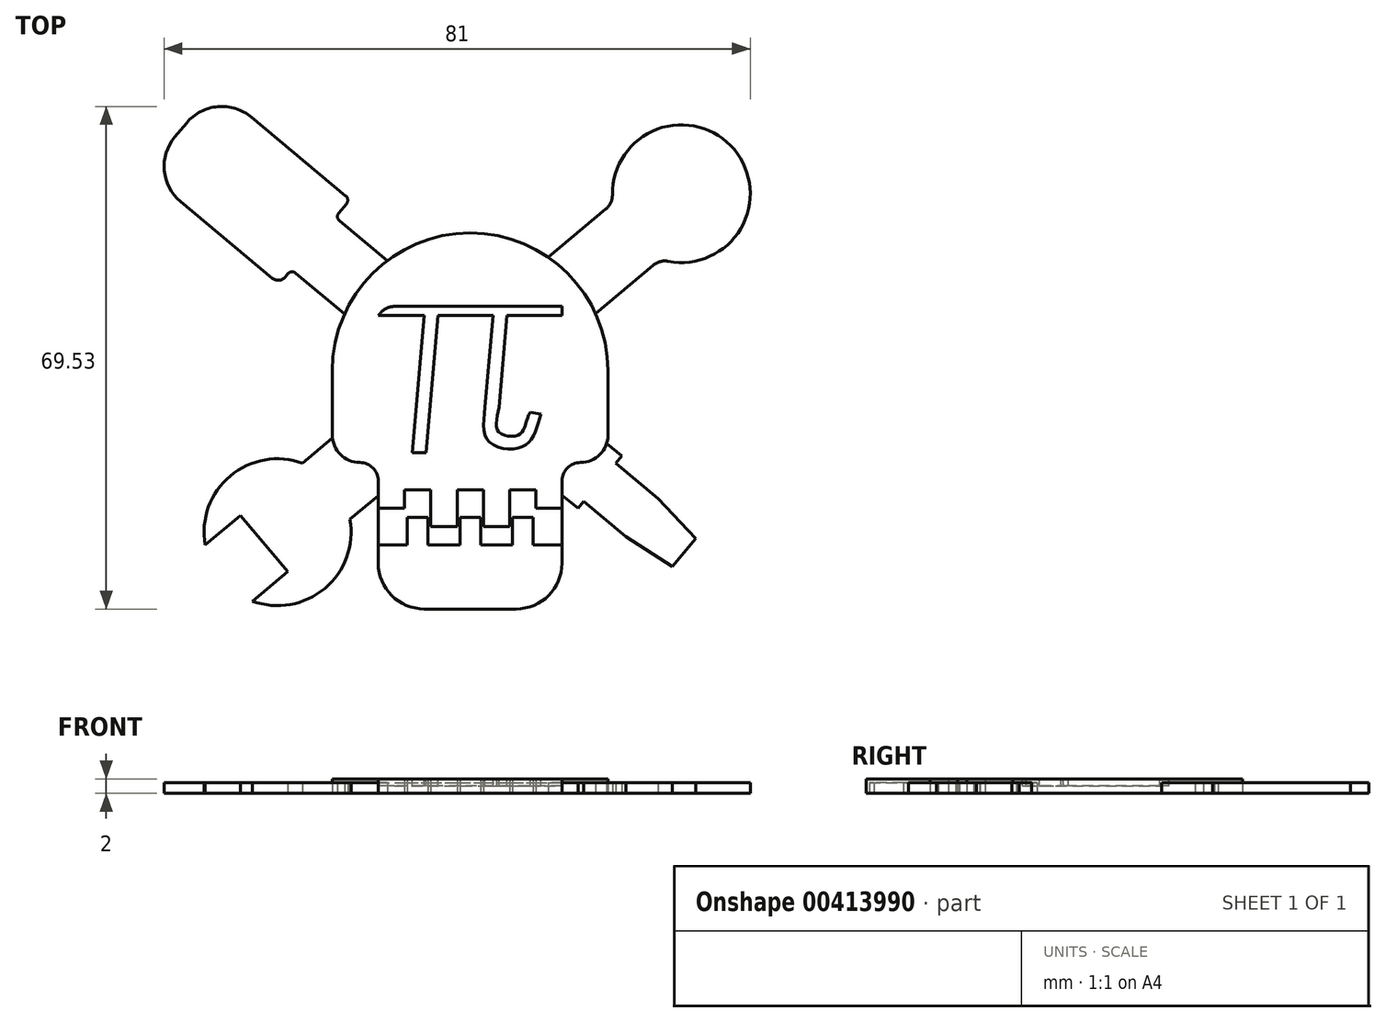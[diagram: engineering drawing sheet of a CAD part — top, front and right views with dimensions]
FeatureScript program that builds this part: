
annotation { "Feature Type Name" : "Feature", "Feature Type Description" : "" }
export const myFeature = defineFeature(function(context is Context, id is Id, definition is map)
    precondition{}
    {
        {
            var Q0;
            Q0=qCreatedBy(makeId("Top.planeOp"),FACE);
            var sketch = newSketch(context, id + "F0", { "sketchPlane" : qUnion([Q0])});
            skLineSegment(sketch, "E0.bottom", {"start": v(0, 19.05) * mm, "end": v(0, 19.05) * mm});
            skLineSegment(sketch, "E0.left", {"start": v(-19.05, 0) * mm, "end": v(-19.05, -8.9) * mm});
            skLineSegment(sketch, "E0.right", {"start": v(19.05, 0) * mm, "end": v(19.05, -8.9) * mm});
            skPoint(sketch, "E0.middle", {"position": v(0, 0) * mm});
            skPoint(sketch, "E1.visualSharp", {"position": v(-19.05, 19.05) * mm});
            skArc(sketch, "E1.filletArc", {"start": v(0, 19.05) * mm, "mid": v(-13.47, 13.47) * mm, "end": v(-19.05, 0) * mm});
            skPoint(sketch, "E2.visualSharp", {"position": v(19.05, 19.05) * mm});
            skArc(sketch, "E2.filletArc", {"start": v(19.05, 0) * mm, "mid": v(13.47, 13.47) * mm, "end": v(0, 19.05) * mm});
            skPoint(sketch, "E3", {"position": v(-19.05, -12.7) * mm});
            skPoint(sketch, "E4", {"position": v(19.05, -12.7) * mm});
            skLineSegment(sketch, "E5", {"start": v(-15.24, -12.7) * mm, "end": v(-15.24, -12.7) * mm});
            skLineSegment(sketch, "E6", {"start": v(15.24, -12.7) * mm, "end": v(15.24, -12.7) * mm});
            skLineSegment(sketch, "E7", {"start": v(-12.7, -15.24) * mm, "end": v(-12.7, -19.05) * mm});
            skLineSegment(sketch, "E8", {"start": v(12.7, -15.24) * mm, "end": v(12.7, -19.05) * mm});
            skArc(sketch, "E9.filletArc", {"start": v(-19.05, -8.9) * mm, "mid": v(-17.93, -11.58) * mm, "end": v(-15.24, -12.7) * mm});
            skArc(sketch, "E10.filletArc", {"start": v(15.24, -12.7) * mm, "mid": v(17.93, -11.58) * mm, "end": v(19.05, -8.9) * mm});
            skPoint(sketch, "E11.visualSharp", {"position": v(-12.7, -12.7) * mm});
            skArc(sketch, "E11.filletArc", {"start": v(-12.7, -15.24) * mm, "mid": v(-13.44, -13.44) * mm, "end": v(-15.24, -12.7) * mm});
            skPoint(sketch, "E12.visualSharp", {"position": v(12.7, -12.7) * mm});
            skArc(sketch, "E12.filletArc", {"start": v(15.24, -12.7) * mm, "mid": v(13.44, -13.44) * mm, "end": v(12.7, -15.24) * mm});
            skLineSegment(sketch, "E13", {"start": v(-12.7, -19.05) * mm, "end": v(-9.07, -19.05) * mm});
            skLineSegment(sketch, "E14", {"start": v(-5.44, -21.6) * mm, "end": v(-1.8, -21.6) * mm});
            skLineSegment(sketch, "E15", {"start": v(1.83, -21.6) * mm, "end": v(5.46, -21.6) * mm});
            skLineSegment(sketch, "E16", {"start": v(9.1, -19.05) * mm, "end": v(12.7, -19.05) * mm});
            skLineSegment(sketch, "E17", {"start": v(-9.07, -19.05) * mm, "end": v(-9.07, -16.51) * mm});
            skLineSegment(sketch, "E18", {"start": v(-9.07, -16.51) * mm, "end": v(-5.44, -16.51) * mm});
            skLineSegment(sketch, "E19", {"start": v(-5.44, -16.51) * mm, "end": v(-5.44, -21.6) * mm});
            skLineSegment(sketch, "E20", {"start": v(-1.8, -21.6) * mm, "end": v(-1.8, -16.51) * mm});
            skLineSegment(sketch, "E21", {"start": v(-1.8, -16.51) * mm, "end": v(1.83, -16.51) * mm});
            skLineSegment(sketch, "E22", {"start": v(1.83, -16.51) * mm, "end": v(1.83, -21.6) * mm});
            skLineSegment(sketch, "E23", {"start": v(5.46, -21.6) * mm, "end": v(5.46, -16.51) * mm});
            skLineSegment(sketch, "E24", {"start": v(5.46, -16.51) * mm, "end": v(9.1, -16.51) * mm});
            skLineSegment(sketch, "E25", {"start": v(9.1, -16.51) * mm, "end": v(9.1, -19.05) * mm});
            skLineSegment(sketch, "E26", {"start": v(25.29, 14.59) * mm, "end": v(-16.62, -20.58) * mm});
            skLineSegment(sketch, "E27", {"start": v(-23.15, -12.8) * mm, "end": v(18.76, 22.37) * mm});
            skLineSegment(sketch, "E28", {"start": v(-24.1, 13.5) * mm, "end": v(14.9, -19.05) * mm});
            skLineSegment(sketch, "E29", {"start": v(20.94, -11.8) * mm, "end": v(-18.06, 20.74) * mm});
            skPoint(sketch, "E30", {"position": v(29.19, 24.5) * mm});
            skArc(sketch, "E31", {"start": v(27.4, 15.13) * mm, "mid": v(36.48, 30.61) * mm, "end": v(19.66, 24.35) * mm});
            skPoint(sketch, "E32.visualSharp", {"position": v(19.75, 23.2) * mm});
            skArc(sketch, "E32.filletArc", {"start": v(18.76, 22.37) * mm, "mid": v(19.43, 23.26) * mm, "end": v(19.66, 24.35) * mm});
            skPoint(sketch, "E33.visualSharp", {"position": v(26.28, 15.42) * mm});
            skArc(sketch, "E33.filletArc", {"start": v(27.4, 15.13) * mm, "mid": v(26.28, 15.1) * mm, "end": v(25.29, 14.59) * mm});
            skLineSegment(sketch, "E34", {"start": v(-17.19, 24.18) * mm, "end": v(-30.25, 35.09) * mm});
            skLineSegment(sketch, "E35", {"start": v(-39.2, 34.28) * mm, "end": v(-40.82, 32.33) * mm});
            skLineSegment(sketch, "E36", {"start": v(-40.01, 23.39) * mm, "end": v(-27.34, 12.8) * mm});
            skLineSegment(sketch, "E37", {"start": v(-25.55, 12.97) * mm, "end": v(-25.18, 13.4) * mm});
            skLineSegment(sketch, "E38.trimOffspring", {"start": v(-18.16, 21.82) * mm, "end": v(-17.09, 23.1) * mm});
            skPoint(sketch, "E39.visualSharp", {"position": v(-35.12, 39.16) * mm});
            skArc(sketch, "E39.filletArc", {"start": v(-30.25, 35.09) * mm, "mid": v(-34.89, 36.54) * mm, "end": v(-39.2, 34.28) * mm});
            skPoint(sketch, "E40.visualSharp", {"position": v(-44.89, 27.46) * mm});
            skArc(sketch, "E40.filletArc", {"start": v(-40.82, 32.33) * mm, "mid": v(-42.27, 27.7) * mm, "end": v(-40.01, 23.39) * mm});
            skPoint(sketch, "E41.visualSharp", {"position": v(-26.36, 12) * mm});
            skArc(sketch, "E41.filletArc", {"start": v(-27.34, 12.8) * mm, "mid": v(-26.41, 12.52) * mm, "end": v(-25.55, 12.97) * mm});
            skPoint(sketch, "E42.visualSharp", {"position": v(-24.7, 14) * mm});
            skArc(sketch, "E42.filletArc", {"start": v(-24.1, 13.5) * mm, "mid": v(-24.66, 13.68) * mm, "end": v(-25.18, 13.4) * mm});
            skPoint(sketch, "E43.visualSharp", {"position": v(-18.65, 21.24) * mm});
            skArc(sketch, "E43.filletArc", {"start": v(-18.16, 21.82) * mm, "mid": v(-18.33, 21.26) * mm, "end": v(-18.06, 20.74) * mm});
            skPoint(sketch, "E44.visualSharp", {"position": v(-16.6, 23.7) * mm});
            skArc(sketch, "E44.filletArc", {"start": v(-17.09, 23.1) * mm, "mid": v(-16.91, 23.66) * mm, "end": v(-17.19, 24.18) * mm});
            skLineSegment(sketch, "E45", {"start": v(14.9, -19.05) * mm, "end": v(20.94, -11.8) * mm});
            skLineSegment(sketch, "E46", {"start": v(20.12, -12.78) * mm, "end": v(25.97, -17.67) * mm});
            skLineSegment(sketch, "E47", {"start": v(31.2, -23.21) * mm, "end": v(27.95, -27.11) * mm});
            skLineSegment(sketch, "E48", {"start": v(21.56, -22.96) * mm, "end": v(15.7, -18.08) * mm});
            skLineSegment(sketch, "E49", {"start": v(21.56, -22.96) * mm, "end": v(27.95, -27.11) * mm});
            skLineSegment(sketch, "E50", {"start": v(25.97, -17.67) * mm, "end": v(31.2, -23.21) * mm});
            skPoint(sketch, "E51", {"position": v(17.92, -15.43) * mm});
            skArc(sketch, "E52", {"start": v(-23.15, -12.8) * mm, "mid": v(-33.15, -14.56) * mm, "end": v(-36.63, -24.1) * mm});
            skLineSegment(sketch, "E53", {"start": v(-23.15, -12.8) * mm, "end": v(-36.63, -24.1) * mm});
            skLineSegment(sketch, "E54", {"start": v(-16.62, -20.58) * mm, "end": v(-30.1, -31.89) * mm});
            skArc(sketch, "E55.trimOffspring", {"start": v(-30.1, -31.89) * mm, "mid": v(-20.1, -30.12) * mm, "end": v(-16.62, -20.58) * mm});
            skLineSegment(sketch, "E56", {"start": v(-31.76, -20.02) * mm, "end": v(-25.23, -27.8) * mm});
            skSolve(sketch);
        }
        {
            var Q0;
            {var subQ6=sQuery(id+"F0.wireOp",EDGE,"E0.left");Q0=makeQuery(id+"F0.imprint","IMPRINT",FACE,{"disambiguationData":[TD([[makeQuery(id+"F0.imprint","IMPRINT",EDGE,{"derivedFrom":subQ6}),1.0]])]});}
            var Q1;
            {var subQ6=sQuery(id+"F0.wireOp",EDGE,"E0.right");Q1=makeQuery(id+"F0.imprint","IMPRINT",FACE,{"disambiguationData":[TD([[makeQuery(id+"F0.imprint","IMPRINT",EDGE,{"derivedFrom":subQ6}),-1.0]])]});}
            var Q2;
            {var subQ0=sQuery(id+"F0.wireOp",EDGE,"E2.filletArc");var subQ1=sQuery(id+"F0.wireOp",EDGE,"E1.filletArc");var subQ2=makeQuery(id+"F0.imprint","INTERSECT",VERTEX,{"derivedFrom":[subQ1,subQ0]});Q2=makeQuery(id+"F0.imprint","IMPRINT",FACE,{"disambiguationData":[TD([[makeQuery(id+"F0.imprint","IMPRINT",EDGE,{"disambiguationData":[TD([[subQ2,-1.0]])],"derivedFrom":subQ1}),1.0]])]});}
            var Q3;
            {var subQ6=sQuery(id+"F0.wireOp",EDGE,"E13");Q3=makeQuery(id+"F0.imprint","IMPRINT",FACE,{"disambiguationData":[TD([[makeQuery(id+"F0.imprint","IMPRINT",EDGE,{"derivedFrom":subQ6}),1.0]])]});}
            var Q4;
            {var subQ0=sQuery(id+"F0.wireOp",EDGE,"E29");var subQ1=sQuery(id+"F0.wireOp",EDGE,"E1.filletArc");var subQ2=makeQuery(id+"F0.imprint","INTERSECT",VERTEX,{"derivedFrom":[subQ1,subQ0]});Q4=makeQuery(id+"F0.imprint","IMPRINT",FACE,{"disambiguationData":[TD([[makeQuery(id+"F0.imprint","IMPRINT",EDGE,{"disambiguationData":[TD([[subQ2,-1.0]])],"derivedFrom":subQ1}),1.0]])]});}
            var Q5;
            {var subQ0=sQuery(id+"F0.wireOp",EDGE,"E26");var subQ1=sQuery(id+"F0.wireOp",EDGE,"E2.filletArc");var subQ2=makeQuery(id+"F0.imprint","INTERSECT",VERTEX,{"derivedFrom":[subQ1,subQ0]});Q5=makeQuery(id+"F0.imprint","IMPRINT",FACE,{"disambiguationData":[TD([[makeQuery(id+"F0.imprint","IMPRINT",EDGE,{"disambiguationData":[TD([[subQ2,-1.0]])],"derivedFrom":subQ1}),1.0]])]});}
            var Q6;
            {var subQ5=sQuery(id+"F0.wireOp",EDGE,"E11.filletArc");Q6=makeQuery(id+"F0.imprint","IMPRINT",FACE,{"disambiguationData":[TD([[makeQuery(id+"F0.imprint","IMPRINT",EDGE,{"derivedFrom":subQ5}),-1.0]])]});}
            var Q7;
            {var subQ7=sQuery(id+"F0.wireOp",EDGE,"E12.filletArc");Q7=makeQuery(id+"F0.imprint","IMPRINT",FACE,{"disambiguationData":[TD([[makeQuery(id+"F0.imprint","IMPRINT",EDGE,{"derivedFrom":subQ7}),-1.0]])]});}
            var Q8;
            {var subQ0=sQuery(id+"F0.wireOp",EDGE,"E29");var subQ1=sQuery(id+"F0.wireOp",EDGE,"E26");var subQ2=makeQuery(id+"F0.imprint","INTERSECT",VERTEX,{"derivedFrom":[subQ1,subQ0]});Q8=makeQuery(id+"F0.imprint","IMPRINT",FACE,{"disambiguationData":[TD([[makeQuery(id+"F0.imprint","IMPRINT",EDGE,{"disambiguationData":[TD([[subQ2,-1.0]])],"derivedFrom":subQ1}),-1.0]])]});}
            extrude(context, id + "F1", {"entities" : qUnion([Q0, Q1, Q2, Q3, Q4, Q5, Q6, Q7, Q8]), "depth" : 2 * mm});
        }
        {
            var Q0;
            {var subQ1=sQuery(id+"F0.wireOp",EDGE,"E46");Q0=makeQuery(id+"F0.imprint","IMPRINT",FACE,{"disambiguationData":[TD([[makeQuery(id+"F0.imprint","IMPRINT",EDGE,{"derivedFrom":subQ1}),-1.0]])]});}
            var Q1;
            Q1=makeQuery(id+"F0.imprint","IMPRINT",FACE,{"disambiguationData":[TD([[makeQuery(id+"F0.imprint","IMPRINT",EDGE,{"derivedFrom":sQuery(id+"F0.wireOp",EDGE,"E31")}),1.0]])]});
            var Q2;
            Q2=makeQuery(id+"F0.imprint","IMPRINT",FACE,{"disambiguationData":[TD([[makeQuery(id+"F0.imprint","IMPRINT",EDGE,{"derivedFrom":sQuery(id+"F0.wireOp",EDGE,"E34")}),1.0]])]});
            var Q3;
            {var subQ5=sQuery(id+"F0.wireOp",EDGE,"E11.filletArc");Q3=makeQuery(id+"F0.imprint","IMPRINT",FACE,{"disambiguationData":[TD([[makeQuery(id+"F0.imprint","IMPRINT",EDGE,{"derivedFrom":subQ5}),1.0]])]});}
            var Q4;
            {var subQ0=sQuery(id+"F0.wireOp",EDGE,"E55.trimOffspring");Q4=makeQuery(id+"F0.imprint","IMPRINT",FACE,{"disambiguationData":[TD([[makeQuery(id+"F0.imprint","IMPRINT",EDGE,{"derivedFrom":subQ0}),1.0]])]});}
            var Q5;
            {var subQ0=sQuery(id+"F0.wireOp",EDGE,"E52");Q5=makeQuery(id+"F0.imprint","IMPRINT",FACE,{"disambiguationData":[TD([[makeQuery(id+"F0.imprint","IMPRINT",EDGE,{"derivedFrom":subQ0}),1.0]])]});}
            var Q6;
            {var subQ0=sQuery(id+"F0.wireOp",EDGE,"E12.filletArc");Q6=makeQuery(id+"F0.imprint","IMPRINT",FACE,{"disambiguationData":[TD([[makeQuery(id+"F0.imprint","IMPRINT",EDGE,{"derivedFrom":subQ0}),1.0]])]});}
            extrude(context, id + "F2", {"entities" : qUnion([Q0, Q1, Q2, Q3, Q4, Q5, Q6]), "operationType" : NewBodyOperationType.ADD, "depth" : 1.5 * mm});
        }
        {
            var Q0;
            Q0=makeQuery(id+"F1.opExtrude","CAP_FACE",FACE,{"disambiguationData":[OSD([sQuery(id+"F0.wireOp",EDGE,"E0.left"),sQuery(id+"F0.wireOp",EDGE,"E0.right"),sQuery(id+"F0.wireOp",EDGE,"E1.filletArc"),sQuery(id+"F0.wireOp",EDGE,"E2.filletArc"),sQuery(id+"F0.wireOp",EDGE,"E7"),sQuery(id+"F0.wireOp",EDGE,"E8"),sQuery(id+"F0.wireOp",EDGE,"E9.filletArc"),sQuery(id+"F0.wireOp",EDGE,"E10.filletArc"),sQuery(id+"F0.wireOp",EDGE,"E11.filletArc"),sQuery(id+"F0.wireOp",EDGE,"E12.filletArc"),sQuery(id+"F0.wireOp",EDGE,"E13"),sQuery(id+"F0.wireOp",EDGE,"E14"),sQuery(id+"F0.wireOp",EDGE,"E15"),sQuery(id+"F0.wireOp",EDGE,"E16"),sQuery(id+"F0.wireOp",EDGE,"E17"),sQuery(id+"F0.wireOp",EDGE,"E18"),sQuery(id+"F0.wireOp",EDGE,"E19"),sQuery(id+"F0.wireOp",EDGE,"E20"),sQuery(id+"F0.wireOp",EDGE,"E21"),sQuery(id+"F0.wireOp",EDGE,"E22"),sQuery(id+"F0.wireOp",EDGE,"E23"),sQuery(id+"F0.wireOp",EDGE,"E24"),sQuery(id+"F0.wireOp",EDGE,"E25")])],"isStart":false});
            var sketch = newSketch(context, id + "F3", { "sketchPlane" : qUnion([Q0])});
            skLineSegment(sketch, "E57", {"start": v(-10.45, 8.9) * mm, "end": v(12.7, 8.9) * mm});
            skLineSegment(sketch, "E58", {"start": v(12.7, 8.9) * mm, "end": v(12.7, 7.62) * mm});
            skLineSegment(sketch, "E59", {"start": v(12.7, 7.62) * mm, "end": v(5.08, 7.62) * mm});
            skLineSegment(sketch, "E60", {"start": v(-12.39, 7.99) * mm, "end": v(-12.7, 7.62) * mm});
            skPoint(sketch, "E61.visualSharp", {"position": v(-11.63, 8.9) * mm});
            skArc(sketch, "E61.filletArc", {"start": v(-10.45, 8.9) * mm, "mid": v(-11.52, 8.65) * mm, "end": v(-12.39, 7.99) * mm});
            skLineSegment(sketch, "E62", {"start": v(-4.45, 7.62) * mm, "end": v(-6.1, -11.36) * mm});
            skLineSegment(sketch, "E63", {"start": v(-6.1, -11.36) * mm, "end": v(-8.01, -11.36) * mm});
            skLineSegment(sketch, "E64", {"start": v(-8.01, -11.36) * mm, "end": v(-6.35, 7.62) * mm});
            skLineSegment(sketch, "E65", {"start": v(3.18, 7.62) * mm, "end": v(2.07, -5.03) * mm});
            skLineSegment(sketch, "E66", {"start": v(5.08, 7.62) * mm, "end": v(3.97, -5.03) * mm});
            skFitSpline(sketch, "E67", {"points": [v(2.07, -5.03) * mm, v(2.44, -9.64) * mm, v(6.19, -10.81) * mm, v(8.6, -9.29) * mm, v(9.8, -5.99) * mm], "startDerivative": vector(-2.55, -20.67) * mm, "endDerivative": vector(5.73, 14.8) * mm});
            skFitSpline(sketch, "E68", {"points": [v(3.97, -5.03) * mm, v(3.93, -8.44) * mm, v(6.62, -8.9) * mm, v(7.57, -7.69) * mm, v(8.3, -5.73) * mm], "startDerivative": vector(-1.95, -13.67) * mm, "endDerivative": vector(5.78, 10.73) * mm});
            skLineSegment(sketch, "E69", {"start": v(8.3, -5.73) * mm, "end": v(9.8, -5.99) * mm});
            skLineSegment(sketch, "E70.trimOffspring", {"start": v(-6.35, 7.62) * mm, "end": v(-12.7, 7.62) * mm});
            skLineSegment(sketch, "E71.trimOffspring", {"start": v(3.18, 7.62) * mm, "end": v(-4.44, 7.62) * mm});
            skSolve(sketch);
        }
        {
            var Q0;
            Q0 = qSketchRegion(id + "F3", true);
            extrude(context, id + "F4", {"entities" : qUnion([Q0]), "operationType" : NewBodyOperationType.REMOVE, "oppositeDirection" : true, "depth" : 1 * mm});
        }
        {
            var Q0;
            {var subQ0=sQuery(id+"F0.wireOp",EDGE,"E29");var subQ1=sQuery(id+"F0.wireOp",EDGE,"E28");var subQ2=sQuery(id+"F0.wireOp",EDGE,"E12.filletArc");var subQ3=sQuery(id+"F0.wireOp",EDGE,"E10.filletArc");var subQ4=sQuery(id+"F0.wireOp",EDGE,"E8");var subQ5=sQuery(id+"F0.wireOp",EDGE,"E27");var subQ6=sQuery(id+"F0.wireOp",EDGE,"E26");var subQ7=sQuery(id+"F0.wireOp",EDGE,"E11.filletArc");var subQ8=sQuery(id+"F0.wireOp",EDGE,"E9.filletArc");var subQ9=sQuery(id+"F0.wireOp",EDGE,"E7");var subQ10=sQuery(id+"F0.wireOp",EDGE,"E2.filletArc");var subQ11=sQuery(id+"F0.wireOp",EDGE,"E1.filletArc");Q0=makeQuery(id+"F2.boolean.opBoolean","MERGE",FACE,{"derivedFrom":[makeQuery(id+"F1.opExtrude","CAP_FACE",FACE,{"disambiguationData":[OSD([sQuery(id+"F0.wireOp",EDGE,"E0.left"),sQuery(id+"F0.wireOp",EDGE,"E0.right"),subQ11,subQ10,subQ9,subQ4,subQ8,subQ3,subQ7,subQ2,sQuery(id+"F0.wireOp",EDGE,"E13"),sQuery(id+"F0.wireOp",EDGE,"E14"),sQuery(id+"F0.wireOp",EDGE,"E15"),sQuery(id+"F0.wireOp",EDGE,"E16"),sQuery(id+"F0.wireOp",EDGE,"E17"),sQuery(id+"F0.wireOp",EDGE,"E18"),sQuery(id+"F0.wireOp",EDGE,"E19"),sQuery(id+"F0.wireOp",EDGE,"E20"),sQuery(id+"F0.wireOp",EDGE,"E21"),sQuery(id+"F0.wireOp",EDGE,"E22"),sQuery(id+"F0.wireOp",EDGE,"E23"),sQuery(id+"F0.wireOp",EDGE,"E24"),sQuery(id+"F0.wireOp",EDGE,"E25")])],"isStart":true}),makeQuery(id+"F2.opExtrude","CAP_FACE",FACE,{"disambiguationData":[OSD([subQ11,subQ1,subQ0,sQuery(id+"F0.wireOp",EDGE,"E34"),sQuery(id+"F0.wireOp",EDGE,"E35"),sQuery(id+"F0.wireOp",EDGE,"E36"),sQuery(id+"F0.wireOp",EDGE,"E37"),sQuery(id+"F0.wireOp",EDGE,"E38.trimOffspring"),sQuery(id+"F0.wireOp",EDGE,"E39.filletArc"),sQuery(id+"F0.wireOp",EDGE,"E40.filletArc"),sQuery(id+"F0.wireOp",EDGE,"E41.filletArc"),sQuery(id+"F0.wireOp",EDGE,"E42.filletArc"),sQuery(id+"F0.wireOp",EDGE,"E43.filletArc"),sQuery(id+"F0.wireOp",EDGE,"E44.filletArc")])],"isStart":true}),makeQuery(id+"F2.opExtrude","CAP_FACE",FACE,{"disambiguationData":[OSD([subQ10,subQ6,subQ5,sQuery(id+"F0.wireOp",EDGE,"E31"),sQuery(id+"F0.wireOp",EDGE,"E32.filletArc"),sQuery(id+"F0.wireOp",EDGE,"E33.filletArc")])],"isStart":true}),makeQuery(id+"F2.opExtrude","CAP_FACE",FACE,{"disambiguationData":[OSD([subQ9,subQ8,subQ7,subQ6,subQ5,sQuery(id+"F0.wireOp",EDGE,"E52"),sQuery(id+"F0.wireOp",EDGE,"E53"),sQuery(id+"F0.wireOp",EDGE,"E54"),sQuery(id+"F0.wireOp",EDGE,"E55.trimOffspring"),sQuery(id+"F0.wireOp",EDGE,"E56")])],"isStart":true}),makeQuery(id+"F2.opExtrude","CAP_FACE",FACE,{"disambiguationData":[OSD([subQ4,subQ3,subQ2,subQ1,subQ0,sQuery(id+"F0.wireOp",EDGE,"E45"),sQuery(id+"F0.wireOp",EDGE,"E46"),sQuery(id+"F0.wireOp",EDGE,"E47"),sQuery(id+"F0.wireOp",EDGE,"E48"),sQuery(id+"F0.wireOp",EDGE,"E49"),sQuery(id+"F0.wireOp",EDGE,"E50")])],"isStart":true})]});}
            var sketch = newSketch(context, id + "F5", { "sketchPlane" : qUnion([Q0])});
            skLineSegment(sketch, "E72.bottom", {"start": v(6.35, 32.97) * mm, "end": v(-6.35, 32.97) * mm});
            skLineSegment(sketch, "E72.top", {"start": v(12.7, 24.13) * mm, "end": v(-12.7, 24.13) * mm});
            skLineSegment(sketch, "E72.left", {"start": v(12.7, 26.62) * mm, "end": v(12.7, 24.13) * mm});
            skLineSegment(sketch, "E72.right", {"start": v(-12.7, 26.62) * mm, "end": v(-12.7, 24.13) * mm});
            skPoint(sketch, "E72.middle", {"position": v(0, 28.55) * mm});
            skPoint(sketch, "E73.visualSharp", {"position": v(-12.7, 32.97) * mm});
            skArc(sketch, "E73.filletArc", {"start": v(-6.35, 32.97) * mm, "mid": v(-10.84, 31.1) * mm, "end": v(-12.7, 26.62) * mm});
            skPoint(sketch, "E74.visualSharp", {"position": v(12.7, 32.97) * mm});
            skArc(sketch, "E74.filletArc", {"start": v(12.7, 26.62) * mm, "mid": v(10.84, 31.1) * mm, "end": v(6.35, 32.97) * mm});
            skLineSegment(sketch, "E75", {"start": v(-8.69, 24.13) * mm, "end": v(-8.69, 20.32) * mm});
            skLineSegment(sketch, "E76", {"start": v(-8.69, 20.32) * mm, "end": v(-5.82, 20.32) * mm});
            skLineSegment(sketch, "E77", {"start": v(-5.82, 24.13) * mm, "end": v(-5.82, 20.32) * mm});
            skLineSegment(sketch, "E78", {"start": v(-1.42, 24.13) * mm, "end": v(-1.42, 20.32) * mm});
            skLineSegment(sketch, "E79", {"start": v(-1.42, 20.32) * mm, "end": v(1.45, 20.32) * mm});
            skLineSegment(sketch, "E80", {"start": v(1.45, 20.32) * mm, "end": v(1.45, 24.13) * mm});
            skLineSegment(sketch, "E81", {"start": v(5.84, 24.13) * mm, "end": v(5.84, 20.32) * mm});
            skLineSegment(sketch, "E82", {"start": v(5.84, 20.32) * mm, "end": v(8.71, 20.32) * mm});
            skLineSegment(sketch, "E83", {"start": v(8.71, 20.32) * mm, "end": v(8.71, 24.13) * mm});
            skSolve(sketch);
        }
        {
            var Q0;
            Q0 = qSketchRegion(id + "F5", true);
            extrude(context, id + "F6", {"entities" : qUnion([Q0]), "oppositeDirection" : true, "depth" : 2 * mm});
        }
        {
            var Q0;
            {var subQ0=sQuery(id+"F0.wireOp",EDGE,"E29");var subQ1=sQuery(id+"F0.wireOp",EDGE,"E28");var subQ2=sQuery(id+"F0.wireOp",EDGE,"E12.filletArc");var subQ3=sQuery(id+"F0.wireOp",EDGE,"E10.filletArc");var subQ4=sQuery(id+"F0.wireOp",EDGE,"E8");var subQ5=sQuery(id+"F0.wireOp",EDGE,"E27");var subQ6=sQuery(id+"F0.wireOp",EDGE,"E26");var subQ7=sQuery(id+"F0.wireOp",EDGE,"E11.filletArc");var subQ8=sQuery(id+"F0.wireOp",EDGE,"E9.filletArc");var subQ9=sQuery(id+"F0.wireOp",EDGE,"E7");var subQ10=sQuery(id+"F0.wireOp",EDGE,"E2.filletArc");var subQ11=sQuery(id+"F0.wireOp",EDGE,"E1.filletArc");Q0=makeQuery(id+"F2.boolean.opBoolean","MERGE",FACE,{"derivedFrom":[makeQuery(id+"F1.opExtrude","CAP_FACE",FACE,{"disambiguationData":[OSD([sQuery(id+"F0.wireOp",EDGE,"E0.left"),sQuery(id+"F0.wireOp",EDGE,"E0.right"),subQ11,subQ10,subQ9,subQ4,subQ8,subQ3,subQ7,subQ2,sQuery(id+"F0.wireOp",EDGE,"E13"),sQuery(id+"F0.wireOp",EDGE,"E14"),sQuery(id+"F0.wireOp",EDGE,"E15"),sQuery(id+"F0.wireOp",EDGE,"E16"),sQuery(id+"F0.wireOp",EDGE,"E17"),sQuery(id+"F0.wireOp",EDGE,"E18"),sQuery(id+"F0.wireOp",EDGE,"E19"),sQuery(id+"F0.wireOp",EDGE,"E20"),sQuery(id+"F0.wireOp",EDGE,"E21"),sQuery(id+"F0.wireOp",EDGE,"E22"),sQuery(id+"F0.wireOp",EDGE,"E23"),sQuery(id+"F0.wireOp",EDGE,"E24"),sQuery(id+"F0.wireOp",EDGE,"E25")])],"isStart":true}),makeQuery(id+"F2.opExtrude","CAP_FACE",FACE,{"disambiguationData":[OSD([subQ11,subQ1,subQ0,sQuery(id+"F0.wireOp",EDGE,"E34"),sQuery(id+"F0.wireOp",EDGE,"E35"),sQuery(id+"F0.wireOp",EDGE,"E36"),sQuery(id+"F0.wireOp",EDGE,"E37"),sQuery(id+"F0.wireOp",EDGE,"E38.trimOffspring"),sQuery(id+"F0.wireOp",EDGE,"E39.filletArc"),sQuery(id+"F0.wireOp",EDGE,"E40.filletArc"),sQuery(id+"F0.wireOp",EDGE,"E41.filletArc"),sQuery(id+"F0.wireOp",EDGE,"E42.filletArc"),sQuery(id+"F0.wireOp",EDGE,"E43.filletArc"),sQuery(id+"F0.wireOp",EDGE,"E44.filletArc")])],"isStart":true}),makeQuery(id+"F2.opExtrude","CAP_FACE",FACE,{"disambiguationData":[OSD([subQ10,subQ6,subQ5,sQuery(id+"F0.wireOp",EDGE,"E31"),sQuery(id+"F0.wireOp",EDGE,"E32.filletArc"),sQuery(id+"F0.wireOp",EDGE,"E33.filletArc")])],"isStart":true}),makeQuery(id+"F2.opExtrude","CAP_FACE",FACE,{"disambiguationData":[OSD([subQ9,subQ8,subQ7,subQ6,subQ5,sQuery(id+"F0.wireOp",EDGE,"E52"),sQuery(id+"F0.wireOp",EDGE,"E53"),sQuery(id+"F0.wireOp",EDGE,"E54"),sQuery(id+"F0.wireOp",EDGE,"E55.trimOffspring"),sQuery(id+"F0.wireOp",EDGE,"E56")])],"isStart":true}),makeQuery(id+"F2.opExtrude","CAP_FACE",FACE,{"disambiguationData":[OSD([subQ4,subQ3,subQ2,subQ1,subQ0,sQuery(id+"F0.wireOp",EDGE,"E45"),sQuery(id+"F0.wireOp",EDGE,"E46"),sQuery(id+"F0.wireOp",EDGE,"E47"),sQuery(id+"F0.wireOp",EDGE,"E48"),sQuery(id+"F0.wireOp",EDGE,"E49"),sQuery(id+"F0.wireOp",EDGE,"E50")])],"isStart":true})]});}
            var sketch = newSketch(context, id + "F7", { "sketchPlane" : qUnion([Q0])});
            skLineSegment(sketch, "E84", {"start": v(12.7, 19.05) * mm, "end": v(12.7, 24.13) * mm});
            skLineSegment(sketch, "E85", {"start": v(-12.7, 19.05) * mm, "end": v(-12.7, 24.13) * mm});
            skLineSegment(sketch, "E86", {"start": v(-12.7, 24.13) * mm, "end": v(-8.69, 24.13) * mm});
            skLineSegment(sketch, "E87", {"start": v(-8.69, 24.13) * mm, "end": v(-8.69, 20.32) * mm});
            skLineSegment(sketch, "E88", {"start": v(-8.69, 20.32) * mm, "end": v(-5.82, 20.32) * mm});
            skLineSegment(sketch, "E89", {"start": v(-5.82, 20.32) * mm, "end": v(-5.82, 24.13) * mm});
            skLineSegment(sketch, "E90", {"start": v(-5.82, 24.13) * mm, "end": v(-1.42, 24.13) * mm});
            skLineSegment(sketch, "E91", {"start": v(-1.42, 24.13) * mm, "end": v(-1.42, 20.32) * mm});
            skLineSegment(sketch, "E92", {"start": v(-1.42, 20.32) * mm, "end": v(1.45, 20.32) * mm});
            skLineSegment(sketch, "E93", {"start": v(1.45, 20.32) * mm, "end": v(1.45, 24.13) * mm});
            skLineSegment(sketch, "E94", {"start": v(1.45, 24.13) * mm, "end": v(5.84, 24.13) * mm});
            skLineSegment(sketch, "E95", {"start": v(5.84, 24.13) * mm, "end": v(5.84, 20.32) * mm});
            skLineSegment(sketch, "E96", {"start": v(5.84, 20.32) * mm, "end": v(8.71, 20.32) * mm});
            skLineSegment(sketch, "E97", {"start": v(8.71, 20.32) * mm, "end": v(8.71, 24.13) * mm});
            skLineSegment(sketch, "E98", {"start": v(8.71, 24.13) * mm, "end": v(12.7, 24.13) * mm});
            skLineSegment(sketch, "E99", {"start": v(-12.7, 19.05) * mm, "end": v(-9.07, 19.05) * mm});
            skLineSegment(sketch, "E100", {"start": v(-9.07, 19.05) * mm, "end": v(-9.07, 16.51) * mm});
            skLineSegment(sketch, "E101", {"start": v(-9.07, 16.51) * mm, "end": v(-5.44, 16.51) * mm});
            skLineSegment(sketch, "E102", {"start": v(-5.44, 16.51) * mm, "end": v(-5.44, 21.6) * mm});
            skLineSegment(sketch, "E103", {"start": v(-5.44, 21.6) * mm, "end": v(-1.8, 21.6) * mm});
            skLineSegment(sketch, "E104", {"start": v(-1.8, 21.6) * mm, "end": v(-1.8, 16.51) * mm});
            skLineSegment(sketch, "E105", {"start": v(-1.8, 16.51) * mm, "end": v(1.83, 16.51) * mm});
            skLineSegment(sketch, "E106", {"start": v(1.83, 16.51) * mm, "end": v(1.83, 21.6) * mm});
            skLineSegment(sketch, "E107", {"start": v(1.83, 21.6) * mm, "end": v(5.46, 21.6) * mm});
            skLineSegment(sketch, "E108", {"start": v(5.46, 21.6) * mm, "end": v(5.46, 16.51) * mm});
            skLineSegment(sketch, "E109", {"start": v(5.46, 16.51) * mm, "end": v(9.1, 16.51) * mm});
            skLineSegment(sketch, "E110", {"start": v(9.1, 16.51) * mm, "end": v(9.1, 19.05) * mm});
            skLineSegment(sketch, "E111", {"start": v(9.1, 19.05) * mm, "end": v(12.7, 19.05) * mm});
            skSolve(sketch);
        }
        {
            var Q0;
            Q0 = qSketchRegion(id + "F7", true);
            extrude(context, id + "F8", {"entities" : qUnion([Q0]), "oppositeDirection" : true, "depth" : 1.5 * mm});
        }
    });
